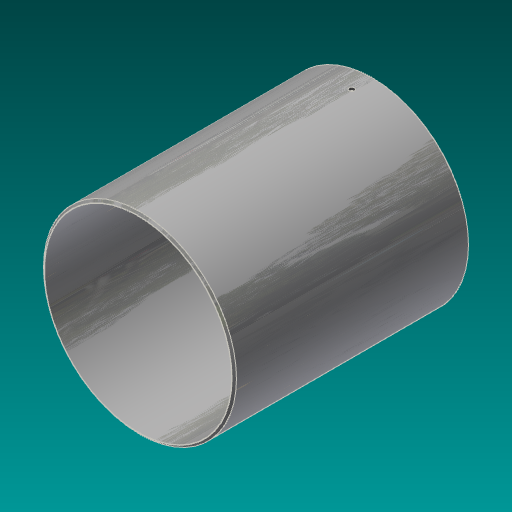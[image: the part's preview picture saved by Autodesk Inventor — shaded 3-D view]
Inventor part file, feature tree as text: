
AUTODESK INVENTOR PART (.ipt)
format: ipt  version: 2017.3 (Build 213257000, 257)  size: 215,552 bytes
history: native  units: in
note: dims shown in document units (in); Inventor stores cm internally (conversion verified against a paired STEP export)
features: chamfer x2, sketch x2, extrude x1, plane x1, hole x1, pattern_circular x1
ambient origin geometry x8: Origin, YZ Plane, XZ Plane, XY Plane, X Axis, Y Axis, Z Axis, Center Point
bodies: Solid1 (feature_tree)
feature tree (8):
  extrude  "Extrusion1"  Depth=33.0in
  chamfer  "Chamfer1"  Distance=41.5536in
  chamfer  "Chamfer2"  Distance=0.125in
  plane  "Work Plane1"
  hole  "Hole1"  [1 undecoded]
  pattern_circular  "Circular Pattern1"  [2 undecoded]
  sketch  "Sketch1"  dims[d0=34.0in d1=33.0in d2=41.5536in d3=0.0in]
  sketch  "Sketch2"  dims[d4=0.4375in d5=0.125in d6=0.2577in d7=0.4375in d8=0.125in d9=0.2577in d10=3.9062in d11=0.891in d12=0.553in d13=0.0246in d14=0.897in d15=0.375in d16=0.25in d17=0.5635in d18=0.91in d19=0.8108in d20=0.7874in d21=360.0deg]
note: 3 required parameter values undecoded (feature->parameter linkage not recoverable at this tier; creation-order binding heuristic only, values carry confidence <= 0.55)
